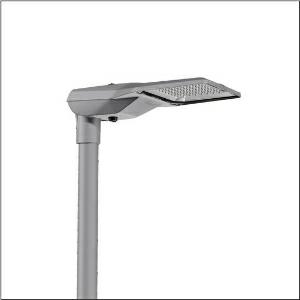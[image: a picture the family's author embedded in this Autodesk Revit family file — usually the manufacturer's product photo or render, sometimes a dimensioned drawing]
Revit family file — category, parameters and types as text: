
# Revit family: streetlight_sl_21_iq_midi___p1_0a_5xe3a31y08mb_7489
name_source: partatom
category: Lighting Fixtures
units: mm (PartAtom-declared; Revit-internal decimal feet)

## family parameters
Cut with Voids When Loaded = No
Host = Face
Light Source = No
Part Type = Normal
Room Calculation Point = No
Round Connector Dimension = Use Diameter
Shared = No

## types (1)
- --- (1 x LED, 18340 lm, 129.3 W, 3000K)
    Apparent Load = 129 VA
    CIE Flux Codes = 21 50 90 100 100
    Color Rendering = 70
    Color Temperature = 3000K
    Default Elevation = 1800 mm
    Description = Streetlight SL 21 iQ midi, mast luminaire, primary light control with lens, of PMMA, primary optical cover: cover, of toughened safety glass, transparent, light distribution: P1.0a, light emission: direct distribution, primary light characteristic: asymmetric, installation type: post-top, side-entry, LED, High Power LED, rated luminous flux: 18.340lm, luminous efficacy: 142lm/W, light colour: 730, colour temperature: 3000K, control gear: iQ-Street Remote, D4i with power reduction, control: pre-setting: logarithmic dimming characteristic, Street-Remote, Auto-Match, Temp-Guard, Lumen-Switch, Night-Set, Smart-Wire, Light-Fading, Desk-Remote (wireless, voltage-free reading and setting of iQ features in the workshop via application-optimized NFC function/RFID function), optimised constant luminous flux control (CLO 2.0), mains connection: 230..240V, AC, 50/60Hz, start of lifetime: 129W, end of service life: 142W, reduction: 56W, luminaire housing, of diecast aluminium, powder-coated, SITECO metallic grey (DB 702S), corrosivity category C5 high according to DIN EN ISO 12944, please order mast flange separately, inclination adjustable: 0°, 5°, 10°, 15°, sealing non-destructively replaceable, multi-level sealing system, length: 644mm, width: 335mm, height: 110mm, mast flange for spigot size: 42mm (side-entry): 5XC10008XM4, 60/48mm (side-entry/post-top): 5XC10108XM2, 76/60mm (side-entry/post-top): 5XC10108XM1, mounting height: 4..8m, Smart Interface below and above, protection rating (complete): IP66, insulation class (complete): insulation class II (safety insulation), certification: CE, ENEC, ENEC+, VDE, impact resistance: IK10, permissible operating ambient temperature for outdoor applications: -40..+50°C, standard-compliant lighting for roads and squares, packaging unit: 1 piece

Light Distribution: P1.0a
    Height = 111 mm
    Lamp = 1 x LED
    Lamp Light Flux = 18340 lm
    Lamp Power = 129.3 W
    Lamp count = 1
    Length = 644 mm
    Luminous efficacy = 142 lm/W
    Manufacturer = Siteco
    ModVariant = No
    Model = 5XE3A31Y08MB
    Number of Poles = 1
    OnlyDefault = Yes
    Power Factor = 1
    Product Name = Streetlight SL 21 iQ midi | P1.0a
    Product group = mast luminaire | pylon top
    ProductGroupID = 6100
    Protection Class = Protection class II
    Protection Degree = IP 66
    RLX_Detail_Level = 1
    RLX_Emergency_Light_Flux = 0 lm
    RLX_Emergency_Type = 0
    RLX_Emergency_Type_DB = No
    RlxData = <blob elided: 101981 chars, md5=f0b895c3>
    Socket = socket
    Standby Power = 0 W
    System Light Flux = 18340 lm
    System Power = 129 W
    Type Comments = factory setting: luminous flux: 100 % | dim-lin: 254 | 672 mA
    Type Image = l_1004304.jpg
    URL = http://relux.com
    VarID = @adj_113585
    Voltage = 0 V
    Weight = 0.00 kg
    Width = 336 mm

## geometry (parser evidence)
native form markers: Blend x4, Sweep x9
no freeform markers — native parametric forms only
